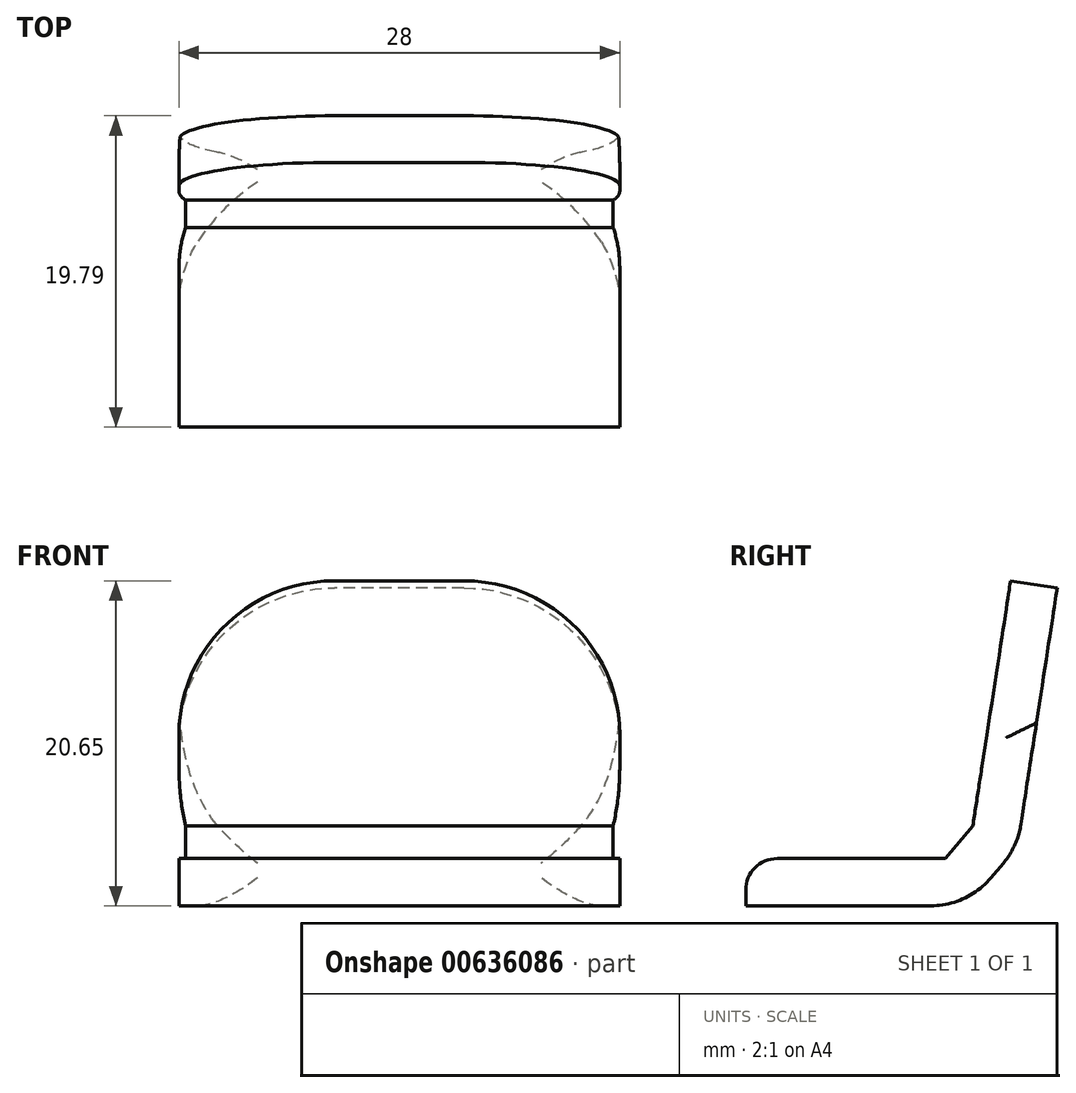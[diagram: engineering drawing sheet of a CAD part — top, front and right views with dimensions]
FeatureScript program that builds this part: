
annotation { "Feature Type Name" : "Feature", "Feature Type Description" : "" }
export const myFeature = defineFeature(function(context is Context, id is Id, definition is map)
    precondition{}
    {
        {
            var Q0;
            Q0=qCreatedBy(makeId("Front.planeOp"),FACE);
            var sketch = newSketch(context, id + "F0", { "sketchPlane" : qUnion([Q0])});
            skLineSegment(sketch, "E0.bottom", {"start": v(14, -1.5) * mm, "end": v(-14, -1.5) * mm});
            skLineSegment(sketch, "E0.top", {"start": v(14, 1.5) * mm, "end": v(-14, 1.5) * mm});
            skLineSegment(sketch, "E0.left", {"start": v(14, -1.5) * mm, "end": v(14, 1.5) * mm});
            skLineSegment(sketch, "E0.right", {"start": v(-14, -1.5) * mm, "end": v(-14, 1.5) * mm});
            skPoint(sketch, "E0.middle", {"position": v(0, 0) * mm});
            skSolve(sketch);
        }
        {
            var Q0;
            Q0=qCreatedBy(makeId("Right.planeOp"),FACE);
            var sketch = newSketch(context, id + "F1", { "sketchPlane" : qUnion([Q0])});
            skLineSegment(sketch, "E1", {"start": v(0, 0) * mm, "end": v(13.38, 0) * mm});
            skLineSegment(sketch, "E2", {"start": v(13.38, 0) * mm, "end": v(15.84, 2.92) * mm});
            skLineSegment(sketch, "E3", {"start": v(15.84, 2.92) * mm, "end": v(18.3, 18.92) * mm});
            skSolve(sketch);
        }
        {
            var Q0;
            Q0=makeQuery(id+"F0.imprint","IMPRINT",FACE,{"disambiguationData":[TD([[makeQuery(id+"F0.imprint","IMPRINT",EDGE,{"derivedFrom":sQuery(id+"F0.wireOp",EDGE,"E0.bottom")}),-1.0]])]});
            var Q1;
            Q1=sQuery(id+"F1.wireOp",EDGE,"E1");
            var Q2;
            Q2=sQuery(id+"F1.wireOp",EDGE,"E2");
            var Q3;
            Q3=sQuery(id+"F1.wireOp",EDGE,"E3");
            sweep(context, id + "F2", {"profiles" : qUnion([Q0]), "path" : qUnion([Q1, Q2, Q3])});
        }
        {
            var Q0;
            Q0=makeQuery(id+"F2.opSweep","CAP_EDGE",EDGE,{"disambiguationData":[OSD([sQuery(id+"F0.wireOp",EDGE,"E0.left"),sQuery(id+"F1.wireOp",VERTEX,"E3.end")])],"isStart":false});
            var Q1;
            Q1=makeQuery(id+"F2.opSweep","CAP_EDGE",EDGE,{"disambiguationData":[OSD([sQuery(id+"F0.wireOp",EDGE,"E0.right"),sQuery(id+"F1.wireOp",VERTEX,"E3.end")])],"isStart":false});
            fillet(context, id + "F3", {"entities" : qUnion([Q0, Q1]), "radius" : 9.9 * mm, "tangentPropagation" : true, "allowEdgeOverflow" : false});
        }
        {
            var Q0;
            Q0=makeQuery(id+"F2.opSweep","CAP_EDGE",EDGE,{"disambiguationData":[OSD([sQuery(id+"F0.wireOp",EDGE,"E0.top"),sQuery(id+"F1.wireOp",VERTEX,"E1.start")])],"isStart":true});
            fillet(context, id + "F4", {"entities" : qUnion([Q0]), "radius" : 2 * mm, "tangentPropagation" : true, "allowEdgeOverflow" : false});
        }
        {
            var Q0;
            Q0=makeQuery(id+"F2.opSweep","SWEPT_FACE",FACE,{"disambiguationData":[OSD([sQuery(id+"F0.wireOp",EDGE,"E0.bottom"),sQuery(id+"F1.wireOp",EDGE,"E2")])]});
            fillet(context, id + "F5", {"entities" : qUnion([Q0]), "radius" : 5 * mm, "tangentPropagation" : true, "allowEdgeOverflow" : false});
        }
    });
